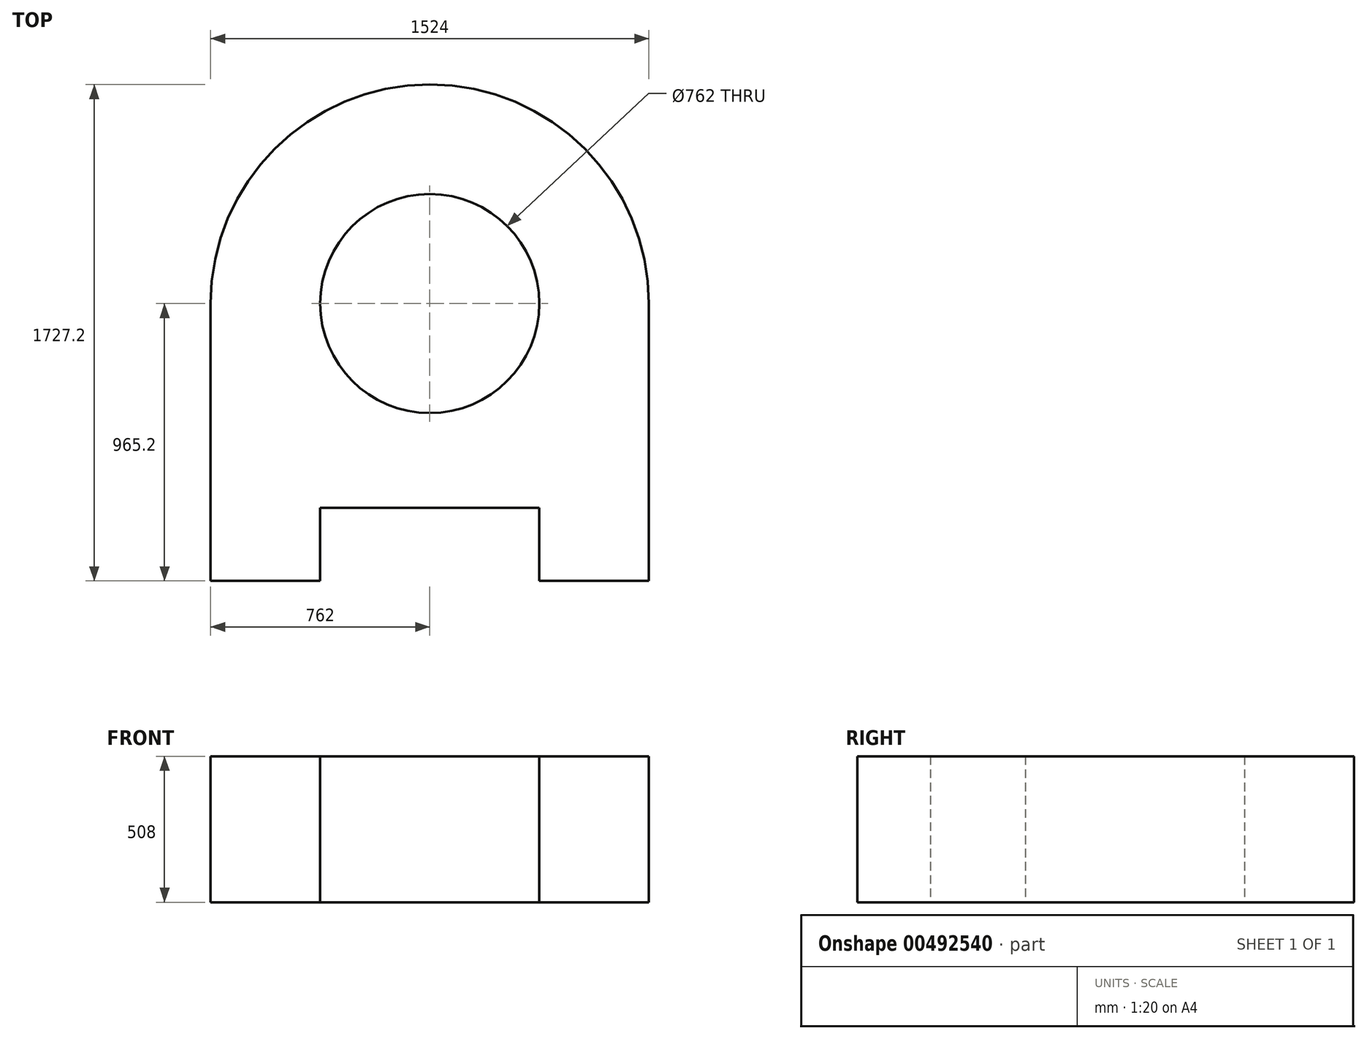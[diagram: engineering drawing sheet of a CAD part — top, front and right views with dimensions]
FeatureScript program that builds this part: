
annotation { "Feature Type Name" : "Feature", "Feature Type Description" : "" }
export const myFeature = defineFeature(function(context is Context, id is Id, definition is map)
    precondition{}
    {
        {
            var Q0;
            Q0=qCreatedBy(makeId("Top.planeOp"),FACE);
            var sketch = newSketch(context, id + "F0", { "sketchPlane" : qUnion([Q0])});
            skLineSegment(sketch, "E0", {"start": v(-381, 0) * mm, "end": v(381, 0) * mm, "construction": true});
            skLineSegment(sketch, "E1", {"start": v(-381, 0) * mm, "end": v(-762, 0) * mm});
            skLineSegment(sketch, "E2", {"start": v(381, 0) * mm, "end": v(762, 0) * mm});
            skLineSegment(sketch, "E3", {"start": v(-381, 0) * mm, "end": v(-381, 254) * mm});
            skLineSegment(sketch, "E4", {"start": v(-381, 254) * mm, "end": v(381, 254) * mm});
            skLineSegment(sketch, "E5", {"start": v(381, 254) * mm, "end": v(381, 0) * mm});
            skLineSegment(sketch, "E6", {"start": v(0, 0) * mm, "end": v(0, 965.2) * mm, "construction": true});
            skArc(sketch, "E7", {"start": v(762, 965.2) * mm, "mid": v(0, 1727.2) * mm, "end": v(-762, 965.2) * mm});
            skLineSegment(sketch, "E8", {"start": v(762, 0) * mm, "end": v(762, 965.2) * mm});
            skLineSegment(sketch, "E9", {"start": v(-762, 0) * mm, "end": v(-762, 965.2) * mm});
            skCircle(sketch, "E10", {"center": v(0, 965.2) * mm, "radius": 381 * mm});
            skSolve(sketch);
        }
        {
            var Q0;
            Q0 = qSketchRegion(id + "F0", true);
            extrude(context, id + "F1", {"entities" : qUnion([Q0]), "depth" : 508 * mm});
        }
    });
